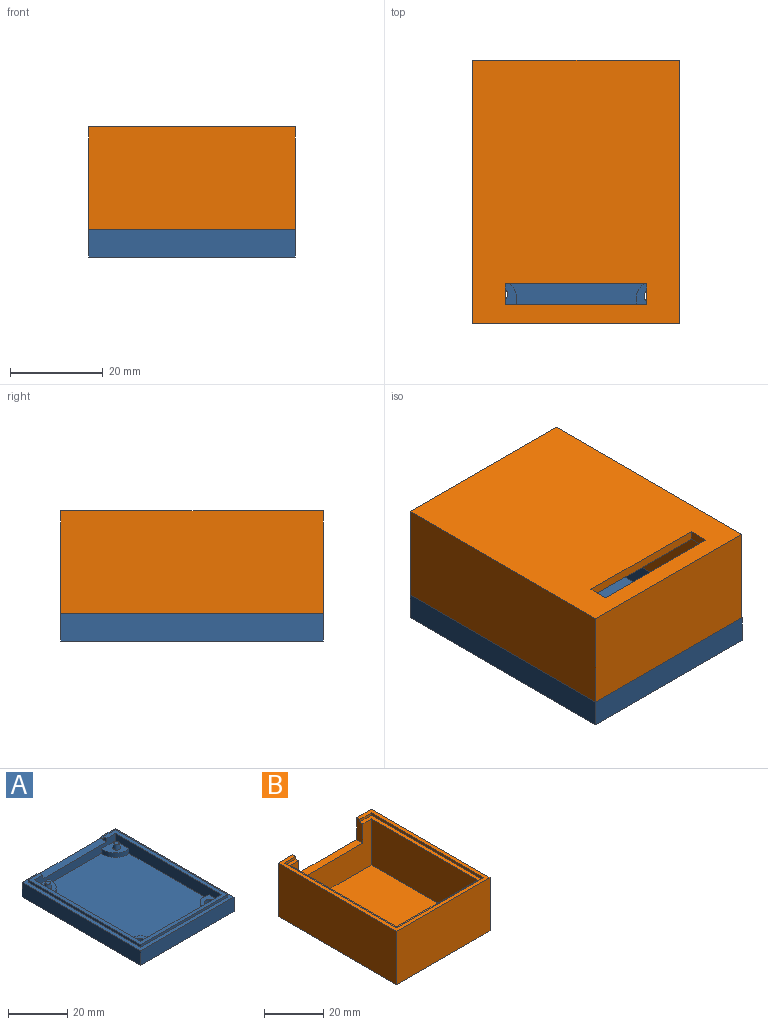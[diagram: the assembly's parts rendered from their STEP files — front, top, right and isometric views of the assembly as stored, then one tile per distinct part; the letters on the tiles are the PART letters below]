
ASSEMBLY  parts=2 mates=1
PART A: 34 faces, bbox 44.5x56.6x7 mm
  f0: plane 53.6x41.5mm, normal (0,0,1), area 230.5mm2, adj f1,f2,f19,f20,f21,f22,f23,f24
  f1: plane 38.5x5mm, normal (0,-1,0), area 120.7mm2, adj f0,f5,f13,f14,f15,f16,f20,f21
  f2: plane 5.5x1mm, normal (0,1,0), area 5.5mm2, adj f0,f4,f23,f29
  f3: plane 44.5x6mm, normal (0,1,0), area 251.7mm2, adj f4,f6,f26,f28,f29,f30,f31
  f4: plane 56.6x44.5mm, normal (0,0,1), area 248.6mm2, adj f2,f3,f22,f23,f24,f25,f26,f27
  f5: plane 50.6x38.5mm, normal (0,0,1), area 1799.5mm2, adj f1,f7,f10,f13,f15,f19,f20,f21
  f6: plane 56.6x44.5mm, normal (0,0,-1), area 2504.6mm2, adj f3,f8,f11,f26,f27,f28
  f7: cylinder r=4.14mm len=6.47mm, axis (0,0,-1), area 22.9mm2, adj f5,f9,f19,f20
  f8: cylinder r=1.5mm len=4mm, axis (0,0,-1), area 37.7mm2, adj f6,f9
  f9: plane 6.47x6.47mm, normal (0,0,1), area 30.1mm2, adj f7,f8,f19,f20
  f10: cylinder r=4.2mm len=6.33mm, axis (0,0,-1), area 22.2mm2, adj f5,f12,f19,f21
  f11: cylinder r=1.5mm len=4mm, axis (0,0,-1), area 37.7mm2, adj f6,f12
  f12: plane 6.33x6.33mm, normal (0,0,1), area 28.5mm2, adj f10,f11,f19,f21
  f13: cylinder r=5.26mm len=6.7mm, axis (0,0,-1), area 22.4mm2, adj f1,f5,f14,f20
  f14: plane 6.7x6.7mm, normal (0,0,1), area 33.5mm2, adj f1,f13,f20,f32
  f15: cylinder r=5.5mm len=6.61mm, axis (0,0,-1), area 21.8mm2, adj f1,f5,f16,f21
  f16: plane 6.61x6.61mm, normal (0,0,1), area 32mm2, adj f1,f15,f21,f33
  f17: plane 1.8x1.8mm, normal (0,0,1), area 2.5mm2, adj f33
  f18: plane 1.8x1.8mm, normal (0,0,1), area 2.5mm2, adj f32
  f19: plane 38.5x5mm, normal (0,1,0), area 169.5mm2, adj f0,f5,f7,f9,f10,f12,f20,f21
  f20: plane 50.6x5mm, normal (1,0,0), area 228.5mm2, adj f0,f1,f5,f7,f9,f13,f14,f19
  f21: plane 50.6x5mm, normal (-1,0,0), area 228.5mm2, adj f0,f1,f5,f10,f12,f15,f16,f19
  f22: plane 5.5x1mm, normal (0,1,0), area 5.5mm2, adj f0,f4,f25,f30
  f23: plane 53.6x1mm, normal (-1,0,0), area 53.6mm2, adj f0,f2,f4,f24
  f24: plane 41.5x1mm, normal (0,-1,0), area 41.5mm2, adj f0,f4,f23,f25
  f25: plane 53.6x1mm, normal (1,0,0), area 53.6mm2, adj f0,f4,f22,f24
  f26: plane 56.6x6mm, normal (-1,0,0), area 339.6mm2, adj f3,f4,f6,f27
  f27: plane 44.5x6mm, normal (0,-1,0), area 267mm2, adj f4,f6,f26,f28
  f28: plane 56.6x6mm, normal (1,0,0), area 339.6mm2, adj f3,f4,f6,f27
  f29: plane 3x1.5mm, normal (1,0,0), area 3mm2, adj f0,f1,f2,f3,f4,f31
  f30: plane 3x1.5mm, normal (-1,0,0), area 3mm2, adj f0,f1,f3,f4,f22,f31
  f31: plane 30.5x3mm, normal (0,0,1), area 91.5mm2, adj f1,f3,f29,f30
  f32: cone r=0.9mm half-angle=11deg, axis (0,0,-1), area 14mm2, adj f14,f18
  f33: cone r=0.9mm half-angle=11deg, axis (0,0,-1), area 14mm2, adj f16,f17
PART B: 24 faces, bbox 44.5x56.6x22 mm
  f0: plane 5.5x1mm, normal (0,-1,0), area 5.5mm2, adj f1,f6,f9,f19
  f1: plane 56.6x44.5mm, normal (0,0,1), area 248.6mm2, adj f0,f8,f9,f10,f11,f12,f13,f14
  f2: plane 38.5x19mm, normal (0,-1,0), area 487.5mm2, adj f3,f5,f6,f7,f17,f18,f19
  f3: plane 50.6x19mm, normal (1,0,0), area 961.4mm2, adj f2,f4,f6,f7
  f4: plane 38.5x19mm, normal (0,1,0), area 731.5mm2, adj f3,f5,f6,f7
  f5: plane 50.6x19mm, normal (-1,0,0), area 961.4mm2, adj f2,f4,f6,f7
  f6: plane 53.6x41.5mm, normal (0,0,1), area 230.5mm2, adj f0,f2,f3,f4,f5,f8,f9,f10
  f7: plane 50.6x38.5mm, normal (0,0,1), area 1810.8mm2, adj f2,f3,f4,f5,f20,f21,f22,f23
  f8: plane 5.5x1mm, normal (0,-1,0), area 5.5mm2, adj f1,f6,f11,f18
  f9: plane 53.6x1mm, normal (1,0,0), area 53.6mm2, adj f0,f1,f6,f10
  f10: plane 41.5x1mm, normal (0,1,0), area 41.5mm2, adj f1,f6,f9,f11
  f11: plane 53.6x1mm, normal (-1,0,0), area 53.6mm2, adj f1,f6,f8,f10
  f12: plane 44.5x22mm, normal (0,1,0), area 704.5mm2, adj f1,f13,f15,f16,f17,f18,f19
  f13: plane 56.6x22mm, normal (-1,0,0), area 1245.2mm2, adj f1,f12,f14,f16
  f14: plane 44.5x22mm, normal (0,-1,0), area 979mm2, adj f1,f13,f15,f16
  f15: plane 56.6x22mm, normal (1,0,0), area 1245.2mm2, adj f1,f12,f14,f16
  f16: plane 56.6x44.5mm, normal (0,0,-1), area 2381.4mm2, adj f12,f13,f14,f15,f20,f21,f22,f23
  f17: plane 30.5x3mm, normal (0,0,1), area 91.5mm2, adj f2,f12,f18,f19
  f18: plane 9x3mm, normal (-1,0,0), area 25.5mm2, adj f1,f2,f6,f8,f12,f17
  f19: plane 9x3mm, normal (1,0,0), area 25.5mm2, adj f0,f1,f2,f6,f12,f17
  f20: plane 30.5x2mm, normal (0,1,0), area 61mm2, adj f7,f16,f21,f23
  f21: plane 4.5x2mm, normal (-1,0,0), area 9mm2, adj f7,f16,f20,f22
  f22: plane 30.5x2mm, normal (0,-1,0), area 61mm2, adj f7,f16,f21,f23
  f23: plane 4.5x2mm, normal (1,0,0), area 9mm2, adj f7,f16,f20,f22
PLACE A t=(-5.64,-21.7,33.82)mm
PLACE B rot(axis=(0,-1,0),180deg) t=(13.58,3.57,61.82)mm
MATE planar A.f4 <-> B.f1  axis (0,0,1) through (13.61,-1.47,39.82)mm
